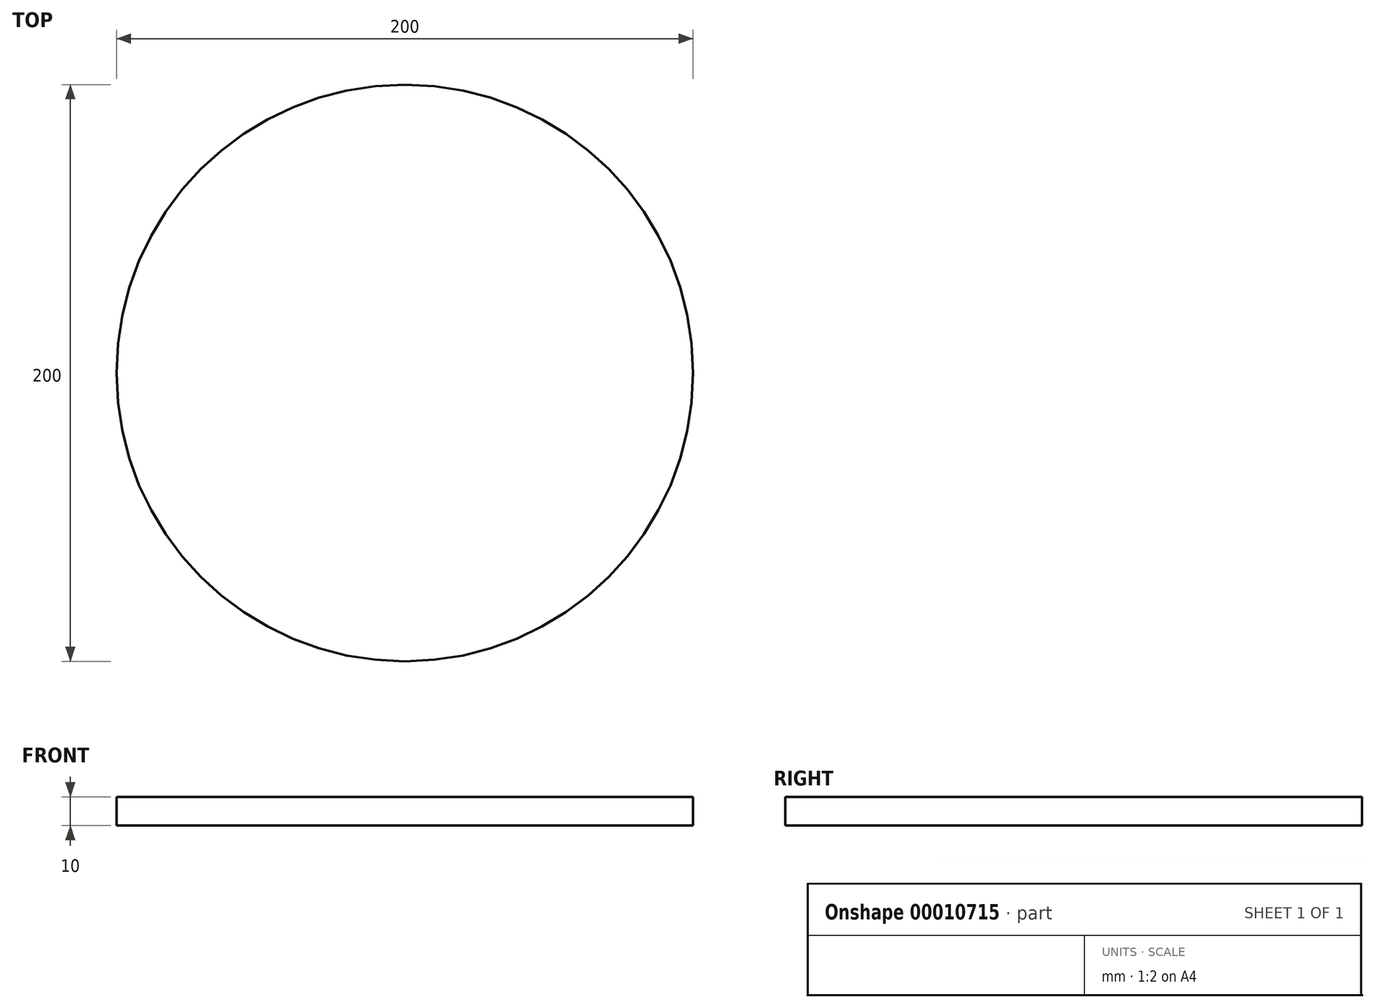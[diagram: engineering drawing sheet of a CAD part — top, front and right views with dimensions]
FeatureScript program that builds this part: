
annotation { "Feature Type Name" : "Feature", "Feature Type Description" : "" }
export const myFeature = defineFeature(function(context is Context, id is Id, definition is map)
    precondition{}
    {
        {
            var Q0;
            Q0=qCreatedBy(makeId("Top.planeOp"),FACE);
            var sketch = newSketch(context, id + "F0", { "sketchPlane" : qUnion([Q0])});
            skCircle(sketch, "E0", {"center": v(0, 0) * mm, "radius": 100 * mm});
            skCircle(sketch, "E1", {"center": v(0, 0) * mm, "radius": 100.55 * mm});
            skSolve(sketch);
        }
        {
            var Q0;
            Q0=makeQuery(id+"F0.imprint","IMPRINT",FACE,{"disambiguationData":[TD([[makeQuery(id+"F0.imprint","IMPRINT",EDGE,{"derivedFrom":sQuery(id+"F0.wireOp",EDGE,"E0")}),1.0]])]});
            extrude(context, id + "F1", {"entities" : qUnion([Q0]), "depth" : 10 * mm});
        }
    });
